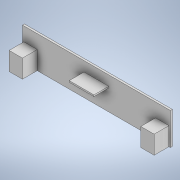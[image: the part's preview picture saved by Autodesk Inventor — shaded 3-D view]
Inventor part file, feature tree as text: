
AUTODESK INVENTOR PART (.ipt)
format: ipt  version: 2020.2 (Build 242310000, 310)  size: 169,984 bytes
history: native  units: mm
features: extrude x4, sketch x4
ambient origin geometry x8: Origin, YZ Plane, XZ Plane, XY Plane, X Axis, Y Axis, Z Axis, Center Point
bodies: Solide1 (feature_tree)
feature tree (8):
  extrude  "Extrusion1"  Depth=300.0mm
  extrude  "Extrusion2"  Depth=65.0mm
  extrude  "Extrusion3"  Depth=4.0mm TaperAngle=0.0deg
  extrude  "Extrusion4"  Depth=30.0mm TaperAngle=0.0deg
  sketch  "Esquisse1"
  sketch  "Esquisse2"
  sketch  "Esquisse3"
  sketch  "Esquisse4"
